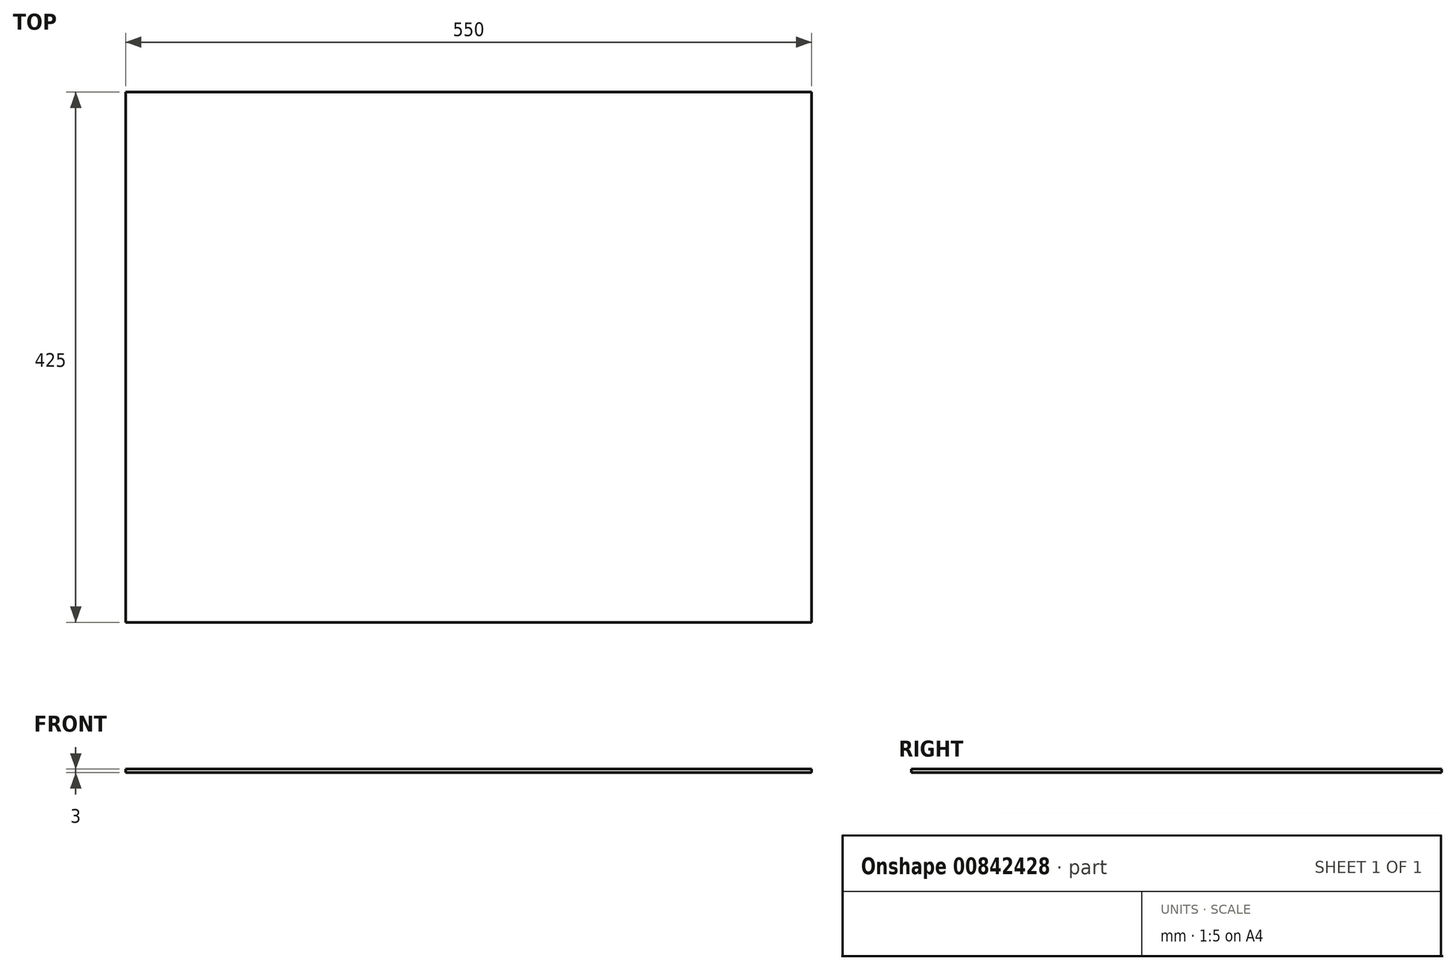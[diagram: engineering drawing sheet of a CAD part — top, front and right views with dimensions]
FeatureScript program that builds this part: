
annotation { "Feature Type Name" : "Feature", "Feature Type Description" : "" }
export const myFeature = defineFeature(function(context is Context, id is Id, definition is map)
    precondition{}
    {
        {
            var Q0;
            Q0=qCreatedBy(makeId("Top.planeOp"),FACE);
            var sketch = newSketch(context, id + "F0", { "sketchPlane" : qUnion([Q0])});
            skLineSegment(sketch, "E0.bottom", {"start": v(275, -212.5) * mm, "end": v(-275, -212.5) * mm});
            skLineSegment(sketch, "E0.top", {"start": v(275, 212.5) * mm, "end": v(-275, 212.5) * mm});
            skLineSegment(sketch, "E0.left", {"start": v(275, -212.5) * mm, "end": v(275, 212.5) * mm});
            skLineSegment(sketch, "E0.right", {"start": v(-275, -212.5) * mm, "end": v(-275, 212.5) * mm});
            skPoint(sketch, "E0.middle", {"position": v(0, 0) * mm});
            skSolve(sketch);
        }
        {
            var Q0;
            Q0=qSketchRegion(id+"F0",true);
            extrude(context, id + "F1", {"entities" : qUnion([Q0]), "depth" : 3 * mm, "offsetDistance" : 25 * mm});
        }
    });
